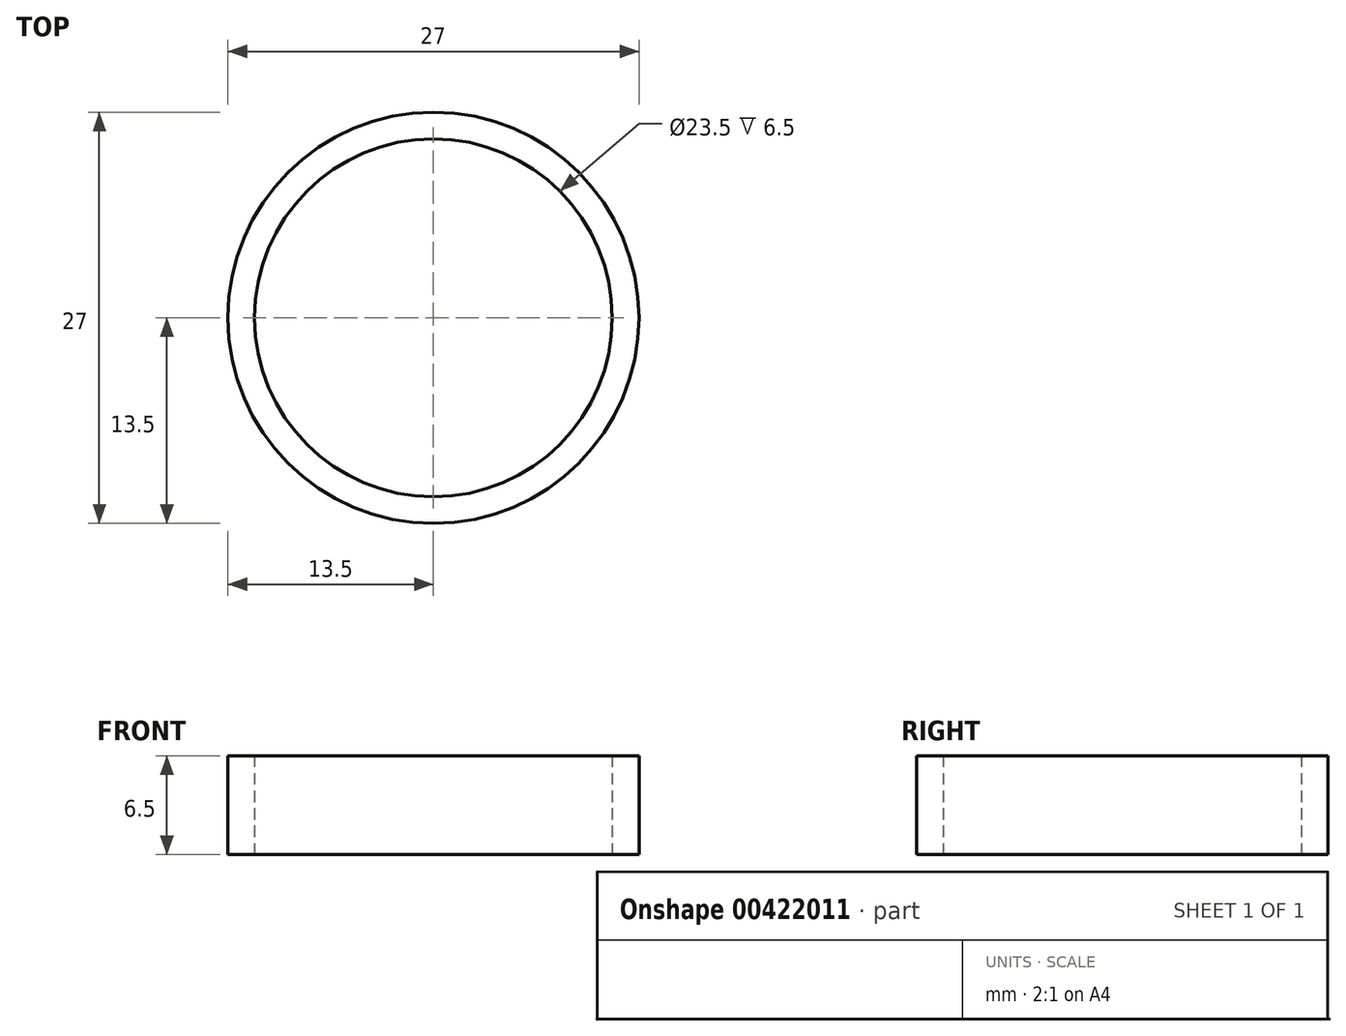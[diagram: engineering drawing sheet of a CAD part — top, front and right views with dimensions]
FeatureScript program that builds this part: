
annotation { "Feature Type Name" : "Feature", "Feature Type Description" : "" }
export const myFeature = defineFeature(function(context is Context, id is Id, definition is map)
    precondition{}
    {
        {
            var Q0;
            Q0=qCreatedBy(makeId("Top.planeOp"),FACE);
            var sketch = newSketch(context, id + "F0", { "sketchPlane" : qUnion([Q0])});
            skCircle(sketch, "E0", {"center": v(0, 0) * mm, "radius": 11.75 * mm});
            skSolve(sketch);
        }
        {
            var Q0;
            Q0=qCreatedBy(makeId("Top.planeOp"),FACE);
            var sketch = newSketch(context, id + "F1", { "sketchPlane" : qUnion([Q0])});
            skCircle(sketch, "E1", {"center": v(0, 0) * mm, "radius": 13.5 * mm});
            skSolve(sketch);
        }
        {
            var Q0;
            Q0 = qSketchRegion(id + "F1", true);
            extrude(context, id + "F2", {"entities" : qUnion([Q0]), "depth" : 6.5 * mm, "offsetDistance" : 25 * mm});
        }
        {
            var Q0;
            Q0 = qSketchRegion(id + "F0", true);
            extrude(context, id + "F3", {"entities" : qUnion([Q0]), "operationType" : NewBodyOperationType.REMOVE, "depth" : 25 * mm, "offsetDistance" : 25 * mm});
        }
    });
